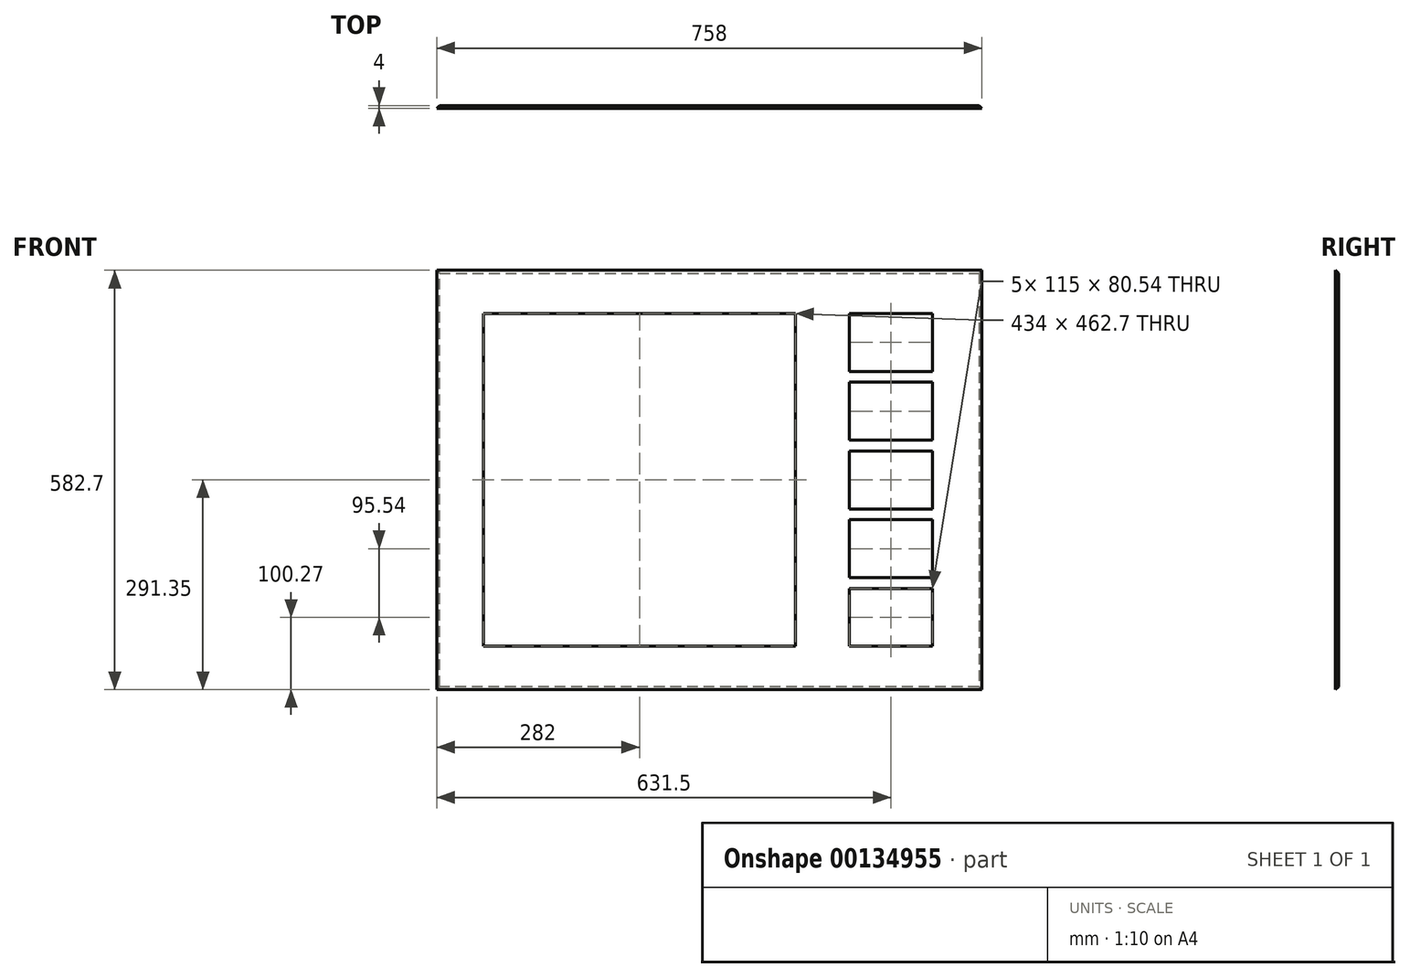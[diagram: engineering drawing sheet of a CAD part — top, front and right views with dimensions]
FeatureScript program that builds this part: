
annotation { "Feature Type Name" : "Feature", "Feature Type Description" : "" }
export const myFeature = defineFeature(function(context is Context, id is Id, definition is map)
    precondition{}
    {
        {
            var Q0;
            Q0=qCreatedBy(makeId("Front.planeOp"),FACE);
            var sketch = newSketch(context, id + "F0", { "sketchPlane" : qUnion([Q0])});
            skLineSegment(sketch, "E0.bottom", {"start": v(0, 0) * mm, "end": v(758, 0) * mm});
            skLineSegment(sketch, "E0.top", {"start": v(0, 582.7) * mm, "end": v(758, 582.7) * mm});
            skLineSegment(sketch, "E0.left", {"start": v(0, 0) * mm, "end": v(0, 582.7) * mm});
            skLineSegment(sketch, "E0.right", {"start": v(758, 0) * mm, "end": v(758, 582.7) * mm});
            skLineSegment(sketch, "E1.bottom", {"start": v(65, 522.7) * mm, "end": v(499, 522.7) * mm});
            skLineSegment(sketch, "E1.top", {"start": v(65, 60) * mm, "end": v(499, 60) * mm});
            skLineSegment(sketch, "E1.left", {"start": v(65, 522.7) * mm, "end": v(65, 60) * mm});
            skLineSegment(sketch, "E1.right", {"start": v(499, 522.7) * mm, "end": v(499, 60) * mm});
            skLineSegment(sketch, "E2.bottom", {"start": v(559, 0) * mm, "end": v(509, 0) * mm});
            skLineSegment(sketch, "E2.top", {"start": v(559, 582.7) * mm, "end": v(509, 582.7) * mm});
            skLineSegment(sketch, "E2.left", {"start": v(559, 0) * mm, "end": v(559, 582.7) * mm, "construction": true});
            skLineSegment(sketch, "E2.right", {"start": v(509, 0) * mm, "end": v(509, 582.7) * mm, "construction": true});
            skLineSegment(sketch, "E3.bottom", {"start": v(574, 522.7) * mm, "end": v(689, 522.7) * mm});
            skLineSegment(sketch, "E3.top", {"start": v(574, 442.16) * mm, "end": v(689, 442.16) * mm});
            skLineSegment(sketch, "E3.left", {"start": v(574, 522.7) * mm, "end": v(574, 442.16) * mm});
            skLineSegment(sketch, "E3.right", {"start": v(689, 522.7) * mm, "end": v(689, 442.16) * mm});
            skLineSegment(sketch, "E4.bottom", {"start": v(574, 427.16) * mm, "end": v(689, 427.16) * mm});
            skLineSegment(sketch, "E4.top", {"start": v(574, 346.62) * mm, "end": v(689, 346.62) * mm});
            skLineSegment(sketch, "E4.left", {"start": v(574, 427.16) * mm, "end": v(574, 346.62) * mm});
            skLineSegment(sketch, "E4.right", {"start": v(689, 427.16) * mm, "end": v(689, 346.62) * mm});
            skLineSegment(sketch, "E5.bottom", {"start": v(574, 331.62) * mm, "end": v(689, 331.62) * mm});
            skLineSegment(sketch, "E5.top", {"start": v(574, 251.08) * mm, "end": v(689, 251.08) * mm});
            skLineSegment(sketch, "E5.left", {"start": v(574, 331.62) * mm, "end": v(574, 251.08) * mm});
            skLineSegment(sketch, "E5.right", {"start": v(689, 331.62) * mm, "end": v(689, 251.08) * mm});
            skLineSegment(sketch, "E6.bottom", {"start": v(574, 236.08) * mm, "end": v(689, 236.08) * mm});
            skLineSegment(sketch, "E7.top", {"start": v(574, 155.54) * mm, "end": v(689, 155.54) * mm});
            skLineSegment(sketch, "E8.bottom", {"start": v(574, 140.54) * mm, "end": v(689, 140.54) * mm});
            skLineSegment(sketch, "E8.top", {"start": v(574, 60) * mm, "end": v(689, 60) * mm});
            skLineSegment(sketch, "E8.left", {"start": v(574, 140.54) * mm, "end": v(574, 60) * mm});
            skLineSegment(sketch, "E8.right", {"start": v(689, 140.54) * mm, "end": v(689, 60) * mm});
            skLineSegment(sketch, "E9", {"start": v(574, 236.08) * mm, "end": v(574, 155.54) * mm});
            skLineSegment(sketch, "E10", {"start": v(689, 236.08) * mm, "end": v(689, 155.54) * mm});
            skSolve(sketch);
        }
        {
            var Q0;
            {var subQ4=sQuery(id+"F0.wireOp",EDGE,"E0.left");Q0=makeQuery(id+"F0.imprint","IMPRINT",FACE,{"disambiguationData":[TD([[makeQuery(id+"F0.imprint","IMPRINT",EDGE,{"derivedFrom":subQ4}),-1.0]])]});}
            extrude(context, id + "F1", {"entities" : qUnion([Q0]), "depth" : 4 * mm});
        }
        {
            var Q0;
            Q0=makeQuery(id+"F1.opExtrude","CAP_EDGE",EDGE,{"disambiguationData":[OSD([sQuery(id+"F0.wireOp",EDGE,"E0.bottom"),sQuery(id+"F0.wireOp",EDGE,"E2.bottom")])],"isStart":true});
            var Q1;
            Q1=makeQuery(id+"F1.opExtrude","CAP_EDGE",EDGE,{"disambiguationData":[OSD([sQuery(id+"F0.wireOp",EDGE,"E0.right")])],"isStart":true});
            var Q2;
            Q2=makeQuery(id+"F1.opExtrude","CAP_EDGE",EDGE,{"disambiguationData":[OSD([sQuery(id+"F0.wireOp",EDGE,"E0.left")])],"isStart":true});
            var Q3;
            Q3=makeQuery(id+"F1.opExtrude","CAP_EDGE",EDGE,{"disambiguationData":[OSD([sQuery(id+"F0.wireOp",EDGE,"E0.top"),sQuery(id+"F0.wireOp",EDGE,"E2.top")])],"isStart":true});
            chamfer(context, id + "F2", {"entities" : qUnion([Q0, Q1, Q2, Q3]), "width" : 4 * mm, "tangentPropagation" : true});
        }
    });
